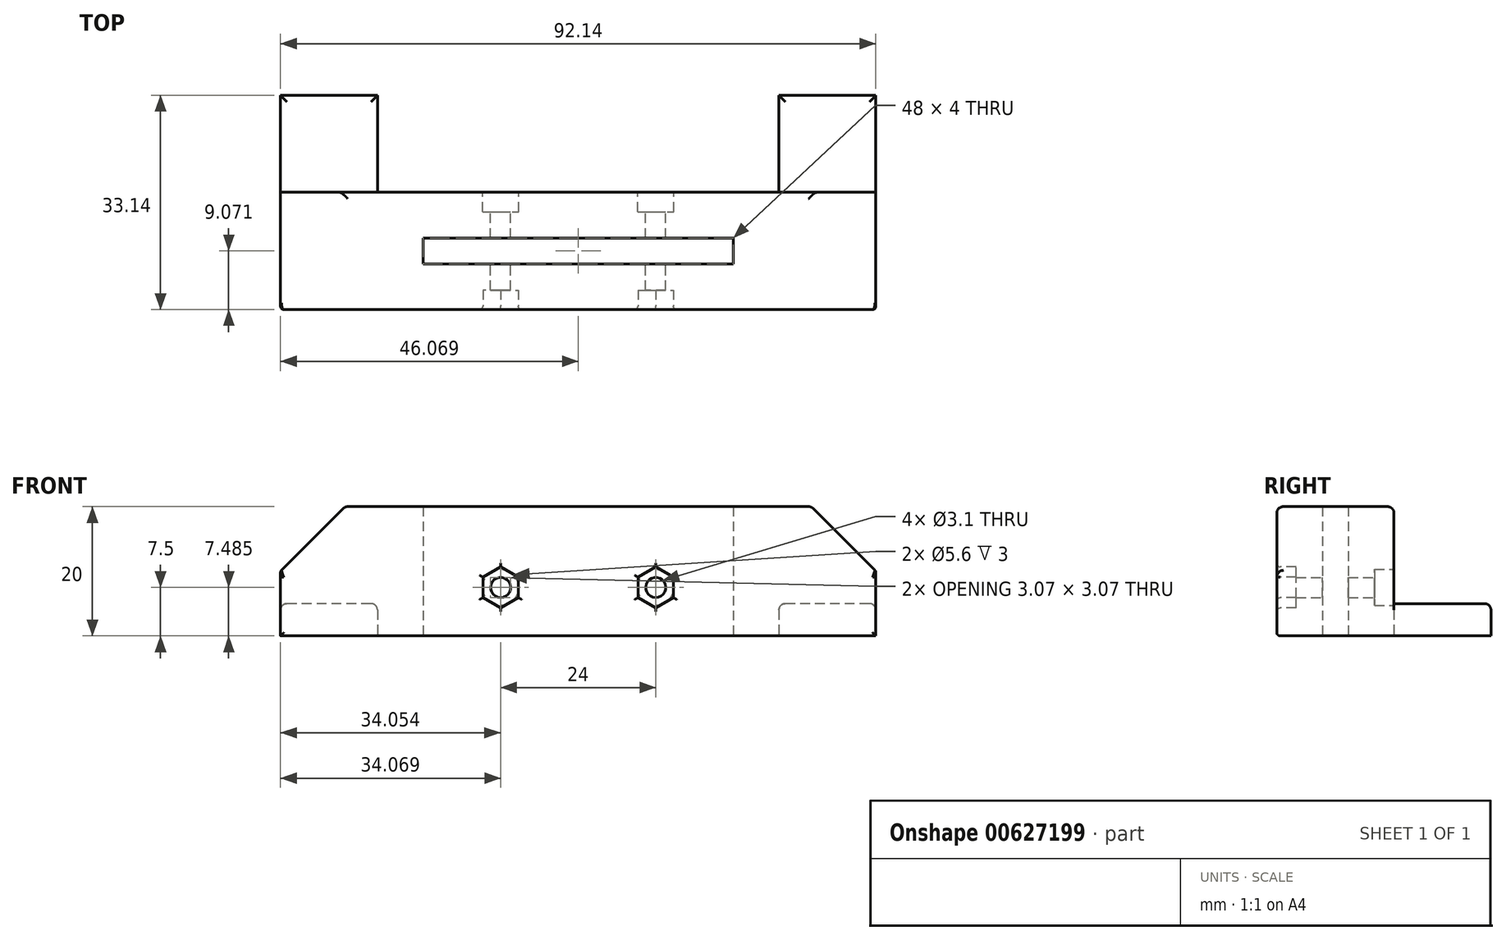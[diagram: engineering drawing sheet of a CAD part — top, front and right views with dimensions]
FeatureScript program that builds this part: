
annotation { "Feature Type Name" : "Feature", "Feature Type Description" : "" }
export const myFeature = defineFeature(function(context is Context, id is Id, definition is map)
    precondition{}
    {
        {
            var Q0;
            Q0=qCreatedBy(makeId("Top.planeOp"),FACE);
            var sketch = newSketch(context, id + "F0", { "sketchPlane" : qUnion([Q0])});
            skLineSegment(sketch, "E0", {"start": v(0, 18.14) * mm, "end": v(0, 0) * mm});
            skLineSegment(sketch, "E1", {"start": v(0, 0) * mm, "end": v(-62.14, 0) * mm});
            skLineSegment(sketch, "E2", {"start": v(-62.14, 0) * mm, "end": v(-62.14, 18.14) * mm});
            skLineSegment(sketch, "E3", {"start": v(-62.14, 18.14) * mm, "end": v(0, 18.14) * mm});
            skLineSegment(sketch, "E4", {"start": v(0, 0) * mm, "end": v(15, 0) * mm});
            skLineSegment(sketch, "E5", {"start": v(-62.14, 0) * mm, "end": v(-77.14, 0) * mm});
            skLineSegment(sketch, "E6", {"start": v(-62.14, 18.14) * mm, "end": v(-77.14, 18.14) * mm});
            skLineSegment(sketch, "E7", {"start": v(-77.14, 18.14) * mm, "end": v(-77.14, 0) * mm});
            skLineSegment(sketch, "E8", {"start": v(15, 0) * mm, "end": v(15, 18.14) * mm});
            skLineSegment(sketch, "E9", {"start": v(15, 18.14) * mm, "end": v(0, 18.14) * mm});
            skLineSegment(sketch, "E10", {"start": v(15, 18.14) * mm, "end": v(15, 33.14) * mm});
            skLineSegment(sketch, "E11", {"start": v(15, 33.14) * mm, "end": v(0, 33.14) * mm});
            skLineSegment(sketch, "E12", {"start": v(0, 33.14) * mm, "end": v(0, 18.14) * mm});
            skLineSegment(sketch, "E13", {"start": v(-77.14, 18.14) * mm, "end": v(-77.14, 33.14) * mm});
            skLineSegment(sketch, "E14", {"start": v(-77.14, 33.14) * mm, "end": v(-62.14, 33.14) * mm});
            skLineSegment(sketch, "E15", {"start": v(-62.14, 33.14) * mm, "end": v(-62.14, 18.14) * mm});
            skLineSegment(sketch, "E16.bottom", {"start": v(-7.07, 7.07) * mm, "end": v(-55.07, 7.07) * mm});
            skLineSegment(sketch, "E16.top", {"start": v(-7.07, 11.07) * mm, "end": v(-55.07, 11.07) * mm});
            skLineSegment(sketch, "E16.left", {"start": v(-7.07, 7.07) * mm, "end": v(-7.07, 11.07) * mm});
            skLineSegment(sketch, "E16.right", {"start": v(-55.07, 7.07) * mm, "end": v(-55.07, 11.07) * mm});
            skPoint(sketch, "E16.middle", {"position": v(-31.07, 9.07) * mm});
            skPoint(sketch, "E16.middle.positionSnap1", {"position": v(-31.07, 18.14) * mm});
            skPoint(sketch, "E16.centerSnap1", {"position": v(-31.07, 18.14) * mm});
            skSolve(sketch);
        }
        {
            var Q0;
            Q0=makeQuery(id+"F0.imprint","IMPRINT",FACE,{"disambiguationData":[TD([[makeQuery(id+"F0.imprint","IMPRINT",EDGE,{"derivedFrom":sQuery(id+"F0.wireOp",EDGE,"E2")}),1.0]])]});
            var Q1;
            Q1=makeQuery(id+"F0.imprint","IMPRINT",FACE,{"disambiguationData":[TD([[makeQuery(id+"F0.imprint","IMPRINT",EDGE,{"derivedFrom":sQuery(id+"F0.wireOp",EDGE,"E0")}),-1.0]])]});
            var Q2;
            Q2=makeQuery(id+"F0.imprint","IMPRINT",FACE,{"disambiguationData":[TD([[makeQuery(id+"F0.imprint","IMPRINT",EDGE,{"derivedFrom":sQuery(id+"F0.wireOp",EDGE,"E0")}),1.0]])]});
            extrude(context, id + "F1", {"entities" : qUnion([Q0, Q1, Q2]), "depth" : 20 * mm, "offsetDistance" : 25 * mm});
        }
        {
            var Q0;
            Q0=makeQuery(id+"F1.opExtrude","SWEPT_FACE",FACE,{"disambiguationData":[OSD([sQuery(id+"F0.wireOp",EDGE,"E1"),sQuery(id+"F0.wireOp",EDGE,"E4"),sQuery(id+"F0.wireOp",EDGE,"E5")])]});
            var sketch = newSketch(context, id + "F2", { "sketchPlane" : qUnion([Q0])});
            skCircle(sketch, "E17", {"center": v(-19.07, 7.5) * mm, "radius": 1.55 * mm});
            skCircle(sketch, "E18", {"center": v(-43.07, 7.5) * mm, "radius": 1.55 * mm});
            skCircle(sketch, "E19.cCircle", {"center": v(-19.07, 7.5) * mm, "radius": 2.75 * mm, "construction": true});
            skLineSegment(sketch, "E19.0", {"start": v(-16.32, 9.09) * mm, "end": v(-16.32, 5.91) * mm});
            skLineSegment(sketch, "E19.1", {"start": v(-16.32, 5.91) * mm, "end": v(-19.07, 4.32) * mm});
            skLineSegment(sketch, "E19.2", {"start": v(-19.07, 4.32) * mm, "end": v(-21.82, 5.91) * mm});
            skLineSegment(sketch, "E19.3", {"start": v(-21.82, 5.91) * mm, "end": v(-21.82, 9.09) * mm});
            skLineSegment(sketch, "E19.4", {"start": v(-21.82, 9.09) * mm, "end": v(-19.07, 10.68) * mm});
            skLineSegment(sketch, "E19.5", {"start": v(-19.07, 10.68) * mm, "end": v(-16.32, 9.09) * mm});
            skPoint(sketch, "E19.0.midPoint", {"position": v(-16.32, 7.5) * mm});
            skLineSegment(sketch, "E20", {"start": v(-31.07, 0) * mm, "end": v(-31.07, 26.32) * mm, "construction": true});
            skLineSegment(sketch, "E21.MirrorCS", {"start": v(-40.32, 9.09) * mm, "end": v(-43.07, 10.68) * mm});
            skCircle(sketch, "E22.MirrorC", {"center": v(-43.07, 7.5) * mm, "radius": 2.75 * mm, "construction": true});
            skLineSegment(sketch, "E23.MirrorCS", {"start": v(-40.32, 5.91) * mm, "end": v(-40.32, 9.09) * mm});
            skLineSegment(sketch, "E24.MirrorCS", {"start": v(-45.82, 5.91) * mm, "end": v(-43.07, 4.32) * mm});
            skLineSegment(sketch, "E25.MirrorCS", {"start": v(-45.82, 9.09) * mm, "end": v(-45.82, 5.91) * mm});
            skLineSegment(sketch, "E26.MirrorCS", {"start": v(-43.07, 4.32) * mm, "end": v(-40.32, 5.91) * mm});
            skLineSegment(sketch, "E27.MirrorCS", {"start": v(-43.07, 10.68) * mm, "end": v(-45.82, 9.09) * mm});
            skLineSegment(sketch, "E28", {"start": v(0, -5.63) * mm, "end": v(0, 19.84) * mm, "construction": true});
            skSolve(sketch);
        }
        {
            var Q0;
            Q0=makeQuery(id+"F0.imprint","IMPRINT",FACE,{"disambiguationData":[TD([[makeQuery(id+"F0.imprint","IMPRINT",EDGE,{"derivedFrom":sQuery(id+"F0.wireOp",EDGE,"E9")}),-1.0]])]});
            var Q1;
            Q1=makeQuery(id+"F0.imprint","IMPRINT",FACE,{"disambiguationData":[TD([[makeQuery(id+"F0.imprint","IMPRINT",EDGE,{"derivedFrom":sQuery(id+"F0.wireOp",EDGE,"E6")}),-1.0]])]});
            extrude(context, id + "F3", {"entities" : qUnion([Q0, Q1]), "operationType" : NewBodyOperationType.ADD, "depth" : 5 * mm, "offsetDistance" : 25 * mm});
        }
        {
            var Q0;
            Q0=makeQuery(id+"F1.opExtrude","CAP_EDGE",EDGE,{"disambiguationData":[OSD([sQuery(id+"F0.wireOp",EDGE,"E8")])],"isStart":false});
            var Q1;
            Q1=makeQuery(id+"F1.opExtrude","CAP_EDGE",EDGE,{"disambiguationData":[OSD([sQuery(id+"F0.wireOp",EDGE,"E7")])],"isStart":false});
            chamfer(context, id + "F4", {"entities" : qUnion([Q0, Q1]), "width" : 10 * mm, "tangentPropagation" : true});
        }
        {
            var Q0;
            Q0=makeQuery(id+"F1.opExtrude","SWEPT_FACE",FACE,{"disambiguationData":[OSD([sQuery(id+"F0.wireOp",EDGE,"E3"),sQuery(id+"F0.wireOp",EDGE,"E6")])]});
            var sketch = newSketch(context, id + "F5", { "sketchPlane" : qUnion([Q0])});
            skLineSegment(sketch, "E29", {"start": v(31.07, 0) * mm, "end": v(31.07, 24.4) * mm, "construction": true});
            skCircle(sketch, "E30", {"center": v(19.07, 7.5) * mm, "radius": 1.55 * mm});
            skCircle(sketch, "E31", {"center": v(43.07, 7.5) * mm, "radius": 1.55 * mm});
            skLineSegment(sketch, "E32", {"start": v(0, 0) * mm, "end": v(0, 24.96) * mm, "construction": true});
            skCircle(sketch, "E33", {"center": v(19.07, 7.5) * mm, "radius": 2.8 * mm});
            skCircle(sketch, "E34.MirrorC", {"center": v(43.07, 7.5) * mm, "radius": 2.8 * mm});
            skSolve(sketch);
        }
        {
            var Q0;
            Q0=makeQuery(id+"F5.imprint","IMPRINT",FACE,{"disambiguationData":[TD([[makeQuery(id+"F5.imprint","IMPRINT",EDGE,{"derivedFrom":sQuery(id+"F5.wireOp",EDGE,"E30")}),1.0]])]});
            var Q1;
            Q1=makeQuery(id+"F5.imprint","IMPRINT",FACE,{"disambiguationData":[TD([[makeQuery(id+"F5.imprint","IMPRINT",EDGE,{"derivedFrom":sQuery(id+"F5.wireOp",EDGE,"E31")}),1.0]])]});
            extrude(context, id + "F6", {"entities" : qUnion([Q0, Q1]), "operationType" : NewBodyOperationType.REMOVE, "oppositeDirection" : true, "depth" : 25 * mm, "offsetDistance" : 25 * mm});
        }
        {
            var Q0;
            Q0=makeQuery(id+"F5.imprint","IMPRINT",FACE,{"disambiguationData":[TD([[makeQuery(id+"F5.imprint","IMPRINT",EDGE,{"derivedFrom":sQuery(id+"F5.wireOp",EDGE,"E30")}),-1.0]])]});
            var Q1;
            Q1=makeQuery(id+"F5.imprint","IMPRINT",FACE,{"disambiguationData":[TD([[makeQuery(id+"F5.imprint","IMPRINT",EDGE,{"derivedFrom":sQuery(id+"F5.wireOp",EDGE,"E31")}),-1.0]])]});
            extrude(context, id + "F7", {"entities" : qUnion([Q0, Q1]), "operationType" : NewBodyOperationType.REMOVE, "oppositeDirection" : true, "depth" : 3 * mm, "offsetDistance" : 25 * mm});
        }
        {
            var Q0;
            Q0=makeQuery(id+"F2.imprint","IMPRINT",FACE,{"disambiguationData":[TD([[makeQuery(id+"F2.imprint","IMPRINT",EDGE,{"derivedFrom":sQuery(id+"F2.wireOp",EDGE,"E17")}),-1.0]])]});
            var Q1;
            Q1=makeQuery(id+"F2.imprint","IMPRINT",FACE,{"disambiguationData":[TD([[makeQuery(id+"F2.imprint","IMPRINT",EDGE,{"derivedFrom":sQuery(id+"F2.wireOp",EDGE,"E18")}),-1.0]])]});
            extrude(context, id + "F8", {"entities" : qUnion([Q0, Q1]), "operationType" : NewBodyOperationType.REMOVE, "oppositeDirection" : true, "depth" : 3 * mm, "offsetDistance" : 25 * mm});
        }
        {
            var Q0;
            {var subQ0=sQuery(id+"F0.wireOp",EDGE,"E7");Q0=makeQuery(id+"F4.opChamfer","BLEND_EDGE",EDGE,{"blendedFrom":[makeQuery(id+"F1.opExtrude","CAP_EDGE",EDGE,{"disambiguationData":[OSD([subQ0])],"isStart":false}),makeQuery(id+"F1.opExtrude","CAP_FACE",FACE,{"disambiguationData":[OSD([sQuery(id+"F0.wireOp",EDGE,"E1"),sQuery(id+"F0.wireOp",EDGE,"E3"),sQuery(id+"F0.wireOp",EDGE,"E4"),sQuery(id+"F0.wireOp",EDGE,"E5"),sQuery(id+"F0.wireOp",EDGE,"E6"),subQ0,sQuery(id+"F0.wireOp",EDGE,"E8"),sQuery(id+"F0.wireOp",EDGE,"E9"),sQuery(id+"F0.wireOp",EDGE,"E16.bottom"),sQuery(id+"F0.wireOp",EDGE,"E16.top"),sQuery(id+"F0.wireOp",EDGE,"E16.left"),sQuery(id+"F0.wireOp",EDGE,"E16.right")])],"isStart":false})],"blendedInto":[makeQuery(id+"F1.opExtrude","CAP_FACE",FACE,{"disambiguationData":[OSD([sQuery(id+"F0.wireOp",EDGE,"E1"),sQuery(id+"F0.wireOp",EDGE,"E3"),sQuery(id+"F0.wireOp",EDGE,"E4"),sQuery(id+"F0.wireOp",EDGE,"E5"),sQuery(id+"F0.wireOp",EDGE,"E6"),subQ0,sQuery(id+"F0.wireOp",EDGE,"E8"),sQuery(id+"F0.wireOp",EDGE,"E9"),sQuery(id+"F0.wireOp",EDGE,"E16.bottom"),sQuery(id+"F0.wireOp",EDGE,"E16.top"),sQuery(id+"F0.wireOp",EDGE,"E16.left"),sQuery(id+"F0.wireOp",EDGE,"E16.right")])],"isStart":false})]});}
            var Q1;
            Q1=makeQuery(id+"F4.opChamfer","BLEND_EDGE",EDGE,{"blendedFrom":[makeQuery(id+"F1.opExtrude","CAP_EDGE",EDGE,{"disambiguationData":[OSD([sQuery(id+"F0.wireOp",EDGE,"E7")])],"isStart":false}),makeQuery(id+"F1.opExtrude","SWEPT_FACE",FACE,{"disambiguationData":[OSD([sQuery(id+"F0.wireOp",EDGE,"E1"),sQuery(id+"F0.wireOp",EDGE,"E4"),sQuery(id+"F0.wireOp",EDGE,"E5")])]})],"blendedInto":[makeQuery(id+"F1.opExtrude","SWEPT_FACE",FACE,{"disambiguationData":[OSD([sQuery(id+"F0.wireOp",EDGE,"E1"),sQuery(id+"F0.wireOp",EDGE,"E4"),sQuery(id+"F0.wireOp",EDGE,"E5")])]})]});
            var Q2;
            Q2=makeQuery(id+"F1.opExtrude","CAP_EDGE",EDGE,{"disambiguationData":[OSD([sQuery(id+"F0.wireOp",EDGE,"E3"),sQuery(id+"F0.wireOp",EDGE,"E6")])],"isStart":false});
            var Q3;
            Q3=makeQuery(id+"F1.opExtrude","CAP_EDGE",EDGE,{"disambiguationData":[OSD([sQuery(id+"F0.wireOp",EDGE,"E1"),sQuery(id+"F0.wireOp",EDGE,"E4"),sQuery(id+"F0.wireOp",EDGE,"E5")])],"isStart":false});
            var Q4;
            Q4=makeQuery(id+"F3.opExtrude","CAP_EDGE",EDGE,{"disambiguationData":[OSD([sQuery(id+"F0.wireOp",EDGE,"E11")])],"isStart":false});
            var Q5;
            Q5=makeQuery(id+"F3.opExtrude","CAP_EDGE",EDGE,{"disambiguationData":[OSD([sQuery(id+"F0.wireOp",EDGE,"E10")])],"isStart":false});
            var Q6;
            Q6=makeQuery(id+"F4.opChamfer","BLEND_EDGE",EDGE,{"blendedFrom":[makeQuery(id+"F1.opExtrude","CAP_EDGE",EDGE,{"disambiguationData":[OSD([sQuery(id+"F0.wireOp",EDGE,"E8")])],"isStart":false}),makeQuery(id+"F1.opExtrude","SWEPT_FACE",FACE,{"disambiguationData":[OSD([sQuery(id+"F0.wireOp",EDGE,"E1"),sQuery(id+"F0.wireOp",EDGE,"E4"),sQuery(id+"F0.wireOp",EDGE,"E5")])]})],"blendedInto":[makeQuery(id+"F1.opExtrude","SWEPT_FACE",FACE,{"disambiguationData":[OSD([sQuery(id+"F0.wireOp",EDGE,"E1"),sQuery(id+"F0.wireOp",EDGE,"E4"),sQuery(id+"F0.wireOp",EDGE,"E5")])]})]});
            var Q7;
            Q7=makeQuery(id+"F3.opExtrude","CAP_EDGE",EDGE,{"disambiguationData":[OSD([sQuery(id+"F0.wireOp",EDGE,"E14")])],"isStart":false});
            var Q8;
            Q8=makeQuery(id+"F3.opExtrude","CAP_EDGE",EDGE,{"disambiguationData":[OSD([sQuery(id+"F0.wireOp",EDGE,"E15")])],"isStart":false});
            var Q9;
            Q9=makeQuery(id+"F3.opExtrude","CAP_EDGE",EDGE,{"disambiguationData":[OSD([sQuery(id+"F0.wireOp",EDGE,"E12")])],"isStart":false});
            var Q10;
            Q10=makeQuery(id+"F3.opExtrude","CAP_EDGE",EDGE,{"disambiguationData":[OSD([sQuery(id+"F0.wireOp",EDGE,"E13")])],"isStart":false});
            var Q11;
            {var subQ0=sQuery(id+"F0.wireOp",EDGE,"E8");Q11=makeQuery(id+"F4.opChamfer","BLEND_EDGE",EDGE,{"blendedFrom":[makeQuery(id+"F1.opExtrude","CAP_EDGE",EDGE,{"disambiguationData":[OSD([subQ0])],"isStart":false}),makeQuery(id+"F1.opExtrude","CAP_FACE",FACE,{"disambiguationData":[OSD([sQuery(id+"F0.wireOp",EDGE,"E1"),sQuery(id+"F0.wireOp",EDGE,"E3"),sQuery(id+"F0.wireOp",EDGE,"E4"),sQuery(id+"F0.wireOp",EDGE,"E5"),sQuery(id+"F0.wireOp",EDGE,"E6"),sQuery(id+"F0.wireOp",EDGE,"E7"),subQ0,sQuery(id+"F0.wireOp",EDGE,"E9"),sQuery(id+"F0.wireOp",EDGE,"E16.bottom"),sQuery(id+"F0.wireOp",EDGE,"E16.top"),sQuery(id+"F0.wireOp",EDGE,"E16.left"),sQuery(id+"F0.wireOp",EDGE,"E16.right")])],"isStart":false})],"blendedInto":[makeQuery(id+"F1.opExtrude","CAP_FACE",FACE,{"disambiguationData":[OSD([sQuery(id+"F0.wireOp",EDGE,"E1"),sQuery(id+"F0.wireOp",EDGE,"E3"),sQuery(id+"F0.wireOp",EDGE,"E4"),sQuery(id+"F0.wireOp",EDGE,"E5"),sQuery(id+"F0.wireOp",EDGE,"E6"),sQuery(id+"F0.wireOp",EDGE,"E7"),subQ0,sQuery(id+"F0.wireOp",EDGE,"E9"),sQuery(id+"F0.wireOp",EDGE,"E16.bottom"),sQuery(id+"F0.wireOp",EDGE,"E16.top"),sQuery(id+"F0.wireOp",EDGE,"E16.left"),sQuery(id+"F0.wireOp",EDGE,"E16.right")])],"isStart":false})]});}
            fillet(context, id + "F9", {"entities" : qUnion([Q0, Q1, Q2, Q3, Q4, Q5, Q6, Q7, Q8, Q9, Q10, Q11]), "radius" : 1 * mm, "tangentPropagation" : true, "allowEdgeOverflow" : false});
        }
        {
            var Q0;
            Q0=makeQuery(id+"F7.boolean.opBoolean","COPY",EDGE,{"derivedFrom":makeQuery(id+"F7.opExtrude","CAP_EDGE",EDGE,{"disambiguationData":[OSD([sQuery(id+"F5.wireOp",EDGE,"E33")])],"isStart":true})});
            var Q1;
            Q1=makeQuery(id+"F7.boolean.opBoolean","COPY",EDGE,{"derivedFrom":makeQuery(id+"F7.opExtrude","CAP_EDGE",EDGE,{"disambiguationData":[OSD([sQuery(id+"F5.wireOp",EDGE,"E34.MirrorC")])],"isStart":true})});
            var Q2;
            Q2=makeQuery(id+"F8.boolean.opBoolean","COPY",EDGE,{"derivedFrom":makeQuery(id+"F8.opExtrude","CAP_EDGE",EDGE,{"disambiguationData":[OSD([sQuery(id+"F2.wireOp",EDGE,"E19.0")])],"isStart":true})});
            var Q3;
            Q3=makeQuery(id+"F8.boolean.opBoolean","COPY",EDGE,{"derivedFrom":makeQuery(id+"F8.opExtrude","CAP_EDGE",EDGE,{"disambiguationData":[OSD([sQuery(id+"F2.wireOp",EDGE,"E19.1")])],"isStart":true})});
            var Q4;
            Q4=makeQuery(id+"F8.boolean.opBoolean","COPY",EDGE,{"derivedFrom":makeQuery(id+"F8.opExtrude","CAP_EDGE",EDGE,{"disambiguationData":[OSD([sQuery(id+"F2.wireOp",EDGE,"E19.2")])],"isStart":true})});
            var Q5;
            Q5=makeQuery(id+"F8.boolean.opBoolean","COPY",EDGE,{"derivedFrom":makeQuery(id+"F8.opExtrude","CAP_EDGE",EDGE,{"disambiguationData":[OSD([sQuery(id+"F2.wireOp",EDGE,"E19.3")])],"isStart":true})});
            var Q6;
            Q6=makeQuery(id+"F1.opExtrude","SWEPT_FACE",FACE,{"disambiguationData":[OSD([sQuery(id+"F0.wireOp",EDGE,"E1"),sQuery(id+"F0.wireOp",EDGE,"E4"),sQuery(id+"F0.wireOp",EDGE,"E5")])]});
            var Q7;
            Q7=makeQuery(id+"F8.boolean.opBoolean","COPY",EDGE,{"derivedFrom":makeQuery(id+"F8.opExtrude","CAP_EDGE",EDGE,{"disambiguationData":[OSD([sQuery(id+"F2.wireOp",EDGE,"E19.5")])],"isStart":true})});
            fillet(context, id + "F10", {"entities" : qUnion([Q0, Q1, Q2, Q3, Q4, Q5, Q6, Q7]), "radius" : 0.5 * mm, "tangentPropagation" : true, "allowEdgeOverflow" : false});
        }
    });
